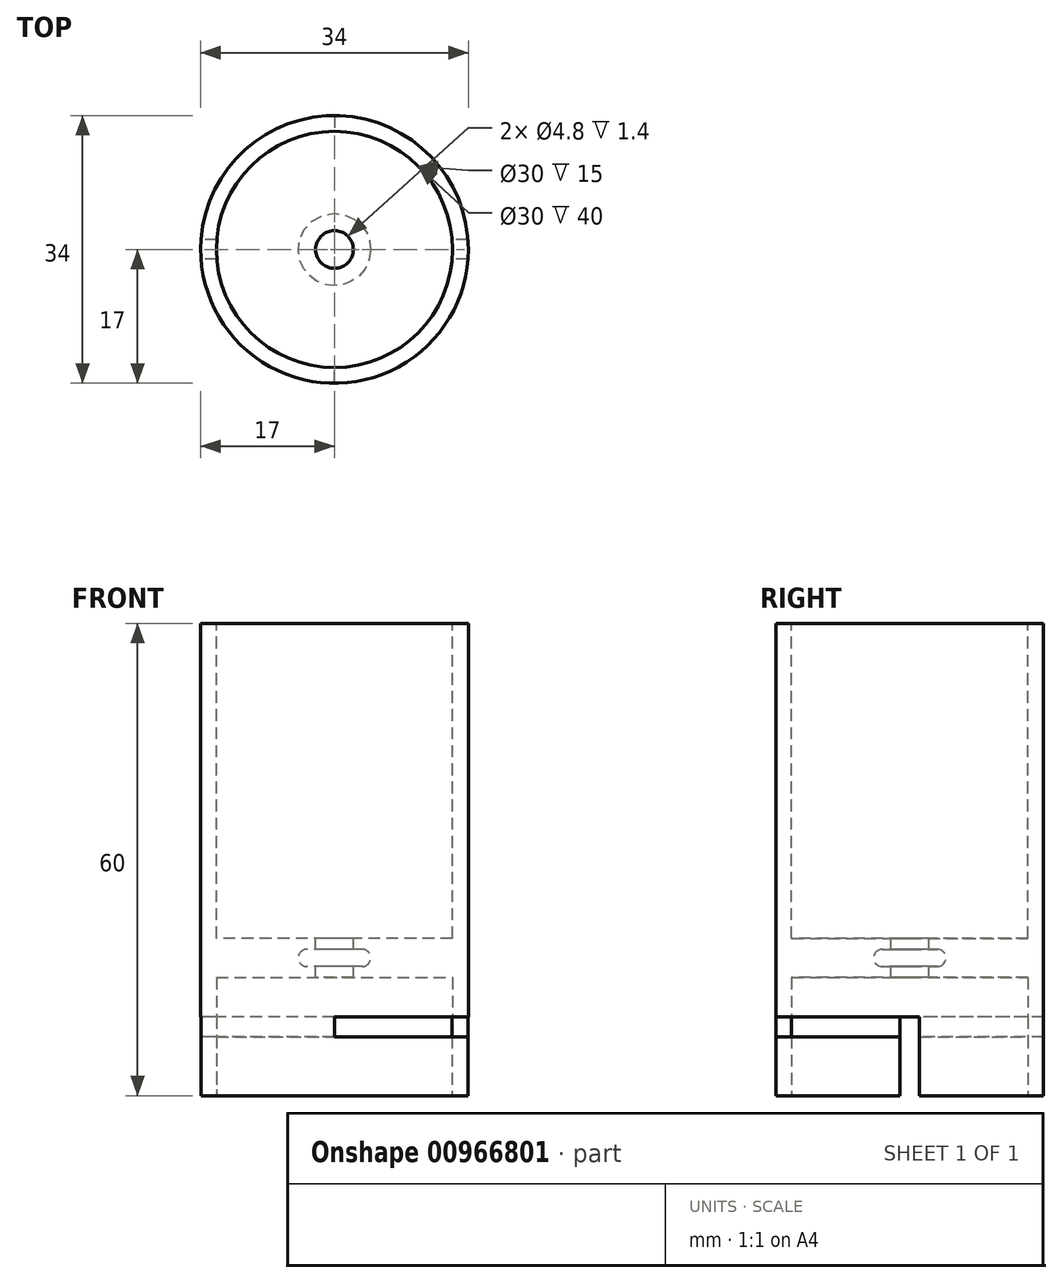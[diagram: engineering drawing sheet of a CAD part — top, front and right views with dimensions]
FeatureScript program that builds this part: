
annotation { "Feature Type Name" : "Feature", "Feature Type Description" : "" }
export const myFeature = defineFeature(function(context is Context, id is Id, definition is map)
    precondition{}
    {
        {
            var Q0;
            Q0=qCreatedBy(makeId("Top.planeOp"),FACE);
            var sketch = newSketch(context, id + "F0", { "sketchPlane" : qUnion([Q0])});
            skCircle(sketch, "E0", {"center": v(0, 0) * mm, "radius": 17 * mm});
            skSolve(sketch);
        }
        {
            var Q0;
            Q0 = qSketchRegion(id + "F0", true);
            extrude(context, id + "F1", {"entities" : qUnion([Q0]), "depth" : 60 * mm, "offsetDistance" : 25.4 * mm});
        }
        {
            var Q0;
            Q0=makeQuery(id+"F1.opExtrude","CAP_FACE",FACE,{"disambiguationData":[OSD([sQuery(id+"F0.wireOp",EDGE,"E0")])],"isStart":false});
            var sketch = newSketch(context, id + "F2", { "sketchPlane" : qUnion([Q0])});
            skCircle(sketch, "E1", {"center": v(0, 0) * mm, "radius": 15 * mm});
            skSolve(sketch);
        }
        {
            var Q0;
            Q0 = qSketchRegion(id + "F2", true);
            extrude(context, id + "F3", {"entities" : qUnion([Q0]), "operationType" : NewBodyOperationType.REMOVE, "oppositeDirection" : true, "depth" : 40 * mm, "offsetDistance" : 25.4 * mm});
        }
        {
            var Q0;
            Q0=makeQuery(id+"F1.opExtrude","CAP_FACE",FACE,{"disambiguationData":[OSD([sQuery(id+"F0.wireOp",EDGE,"E0")])],"isStart":true});
            var sketch = newSketch(context, id + "F4", { "sketchPlane" : qUnion([Q0])});
            skCircle(sketch, "E2", {"center": v(0, 0) * mm, "radius": 15 * mm});
            skSolve(sketch);
        }
        {
            var Q0;
            Q0=makeQuery(id+"F4.imprint","IMPRINT",FACE,{"disambiguationData":[TD([[makeQuery(id+"F4.imprint","IMPRINT",EDGE,{"derivedFrom":sQuery(id+"F4.wireOp",EDGE,"E2")}),1.0]])]});
            extrude(context, id + "F5", {"entities" : qUnion([Q0]), "operationType" : NewBodyOperationType.REMOVE, "oppositeDirection" : true, "depth" : 15 * mm, "offsetDistance" : 25.4 * mm});
        }
        {
            var Q0;
            Q0=qCreatedBy(makeId("Right.planeOp"),FACE);
            var sketch = newSketch(context, id + "F6", { "sketchPlane" : qUnion([Q0])});
            skLineSegment(sketch, "E3.bottom", {"start": v(-1.25, 10) * mm, "end": v(1.25, 10) * mm});
            skLineSegment(sketch, "E3.top", {"start": v(-1.25, 0) * mm, "end": v(1.25, 0) * mm});
            skLineSegment(sketch, "E3.left", {"start": v(-1.25, 10) * mm, "end": v(-1.25, 0) * mm});
            skLineSegment(sketch, "E3.right", {"start": v(1.25, 10) * mm, "end": v(1.25, 0) * mm});
            skSolve(sketch);
        }
        {
            var Q0;
            Q0 = qSketchRegion(id + "F6", true);
            var Q1;
            Q1=makeQuery(id+"F1.opExtrude","SWEPT_FACE",FACE,{"disambiguationData":[OSD([sQuery(id+"F0.wireOp",EDGE,"E0")])]});
            var Q2;
            Q2=makeQuery(id+"F1.opExtrude","SWEPT_FACE",FACE,{"disambiguationData":[OSD([sQuery(id+"F0.wireOp",EDGE,"E0")])]});
            extrude(context, id + "F7", {"entities" : qUnion([Q0]), "operationType" : NewBodyOperationType.REMOVE, "endBound" : BoundingType.UP_TO_SURFACE, "depth" : 25.4 * mm, "endBoundEntityFace" : qUnion([Q1]), "offsetDistance" : 25.4 * mm, "hasSecondDirection" : true, "secondDirectionBound" : SecondDirectionBoundingType.UP_TO_SURFACE, "secondDirectionOppositeDirection" : true, "secondDirectionDepth" : 25.4 * mm, "secondDirectionBoundEntityFace" : qUnion([Q2])});
        }
        {
            var Q0;
            Q0=qCreatedBy(makeId("Front.planeOp"),FACE);
            var sketch = newSketch(context, id + "F8", { "sketchPlane" : qUnion([Q0])});
            skLineSegment(sketch, "E4.bottom", {"start": v(-17, 10) * mm, "end": v(0, 10) * mm});
            skLineSegment(sketch, "E4.top", {"start": v(-17, 7.5) * mm, "end": v(0, 7.5) * mm});
            skLineSegment(sketch, "E4.left", {"start": v(0, 10) * mm, "end": v(0, 7.5) * mm});
            skLineSegment(sketch, "E4.right", {"start": v(-17, 10) * mm, "end": v(-17, 7.5) * mm});
            skLineSegment(sketch, "E5", {"start": v(17, 60) * mm, "end": v(17, 0) * mm, "construction": true});
            skLineSegment(sketch, "E6", {"start": v(0, 0) * mm, "end": v(0, 18.46) * mm, "construction": true});
            skSolve(sketch);
        }
        {
            var Q0;
            Q0=qCreatedBy(makeId("Front.planeOp"),FACE);
            var sketch = newSketch(context, id + "F9", { "sketchPlane" : qUnion([Q0])});
            skLineSegment(sketch, "E7", {"start": v(0, 43.1) * mm, "end": v(0, -11.8) * mm, "construction": true});
            skSolve(sketch);
        }
        {
            var Q0;
            Q0 = qSketchRegion(id + "F8", true);
            var Q1;
            Q1=sQuery(id+"F9.wireOp",EDGE,"E7");
            revolve(context, id + "F10", {"operationType" : NewBodyOperationType.REMOVE, "surfaceOperationType" : NewSurfaceOperationType.NEW, "entities" : qUnion([Q0]), "axis" : qUnion([Q1]), "revolveType" : RevolveType.ONE_DIRECTION, "angle" : 90 * degree});
        }
        {
            var Q0;
            Q0=qCreatedBy(makeId("Front.planeOp"),FACE);
            var sketch = newSketch(context, id + "F11", { "sketchPlane" : qUnion([Q0])});
            skLineSegment(sketch, "E8", {"start": v(0, -0.56) * mm, "end": v(0, 13.62) * mm, "construction": true});
            skLineSegment(sketch, "E9.bottom", {"start": v(17, 10) * mm, "end": v(0, 10) * mm});
            skLineSegment(sketch, "E9.top", {"start": v(17, 7.5) * mm, "end": v(0, 7.5) * mm});
            skLineSegment(sketch, "E9.left", {"start": v(17, 10) * mm, "end": v(17, 7.5) * mm});
            skLineSegment(sketch, "E9.right", {"start": v(0, 10) * mm, "end": v(0, 7.5) * mm});
            skLineSegment(sketch, "E10", {"start": v(-17, 10) * mm, "end": v(-17, 60) * mm});
            skLineSegment(sketch, "E11", {"start": v(17, 60) * mm, "end": v(17, 4.17) * mm, "construction": true});
            skSolve(sketch);
        }
        {
            var Q0;
            Q0 = qSketchRegion(id + "F11", true);
            var Q1;
            Q1=sQuery(id+"F11.wireOp",EDGE,"E8");
            revolve(context, id + "F12", {"operationType" : NewBodyOperationType.REMOVE, "surfaceOperationType" : NewSurfaceOperationType.NEW, "entities" : qUnion([Q0]), "axis" : qUnion([Q1]), "revolveType" : RevolveType.ONE_DIRECTION, "oppositeDirection" : true, "angle" : 90 * degree});
        }
        {
            var Q0;
            Q0=qCreatedBy(makeId("Front.planeOp"),FACE);
            var sketch = newSketch(context, id + "F13", { "sketchPlane" : qUnion([Q0])});
            skLineSegment(sketch, "E12", {"start": v(0, 0) * mm, "end": v(0, 35) * mm, "construction": true});
            skLineSegment(sketch, "E13.0", {"start": v(-15, 20) * mm, "end": v(15, 20) * mm, "construction": true});
            skLineSegment(sketch, "E14.0", {"start": v(15, 15) * mm, "end": v(-15, 15) * mm, "construction": true});
            skLineSegment(sketch, "E15", {"start": v(-17, 10) * mm, "end": v(-17, 60) * mm, "construction": true});
            skLineSegment(sketch, "E16", {"start": v(17, 60) * mm, "end": v(17, 10) * mm, "construction": true});
            skLineSegment(sketch, "E17", {"start": v(0, 15) * mm, "end": v(-2.4, 15) * mm});
            skLineSegment(sketch, "E18", {"start": v(0, 15) * mm, "end": v(0, 20) * mm});
            skLineSegment(sketch, "E19", {"start": v(0, 20) * mm, "end": v(-2.4, 20) * mm});
            skLineSegment(sketch, "E20", {"start": v(-2.4, 16.4) * mm, "end": v(-2.4, 15) * mm});
            skLineSegment(sketch, "E21", {"start": v(-2.4, 20) * mm, "end": v(-2.4, 18.6) * mm});
            skPoint(sketch, "E22", {"position": v(0, 17.5) * mm});
            skLineSegment(sketch, "E23", {"start": v(-2.4, 16.4) * mm, "end": v(-3.5, 16.4) * mm});
            skLineSegment(sketch, "E24", {"start": v(-2.4, 18.6) * mm, "end": v(-3.5, 18.6) * mm});
            skArc(sketch, "E25", {"start": v(-3.5, 18.6) * mm, "mid": v(-4.6, 17.5) * mm, "end": v(-3.5, 16.4) * mm});
            skSolve(sketch);
        }
        {
            var Q0;
            Q0 = qSketchRegion(id + "F13", true);
            var Q1;
            Q1=sQuery(id+"F13.wireOp",EDGE,"E12");
            revolve(context, id + "F14", {"operationType" : NewBodyOperationType.REMOVE, "surfaceOperationType" : NewSurfaceOperationType.NEW, "entities" : qUnion([Q0]), "axis" : qUnion([Q1]), "revolveType" : RevolveType.FULL, "oppositeDirection" : true});
        }
    });
